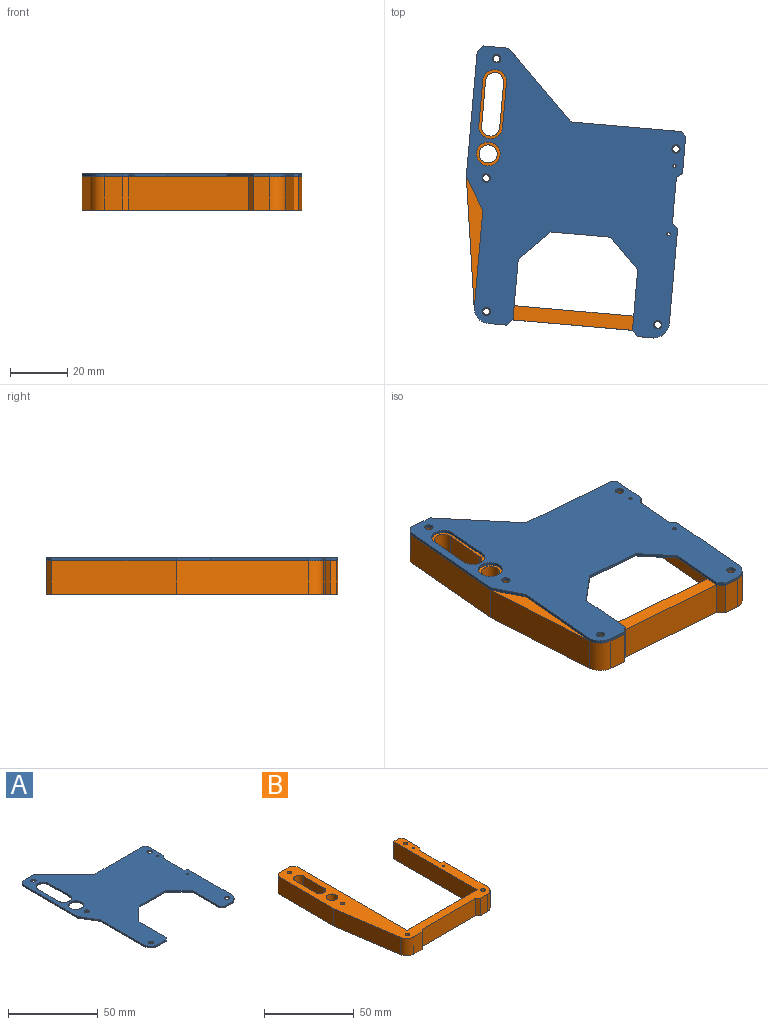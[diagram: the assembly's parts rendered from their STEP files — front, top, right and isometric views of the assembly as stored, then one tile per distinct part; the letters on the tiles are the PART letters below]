
ASSEMBLY  parts=2 mates=1
PART A: 38 faces, bbox 75.4x96.8x1 mm
  f0: plane 5.68x1mm, normal (0,-1,0), area 5.7mm2, adj f2,f3,f15,f37
  f1: plane 12.99x1mm, normal (1,0,0), area 13mm2, adj f2,f3,f17,f28
  f2: plane 96.75x75.4mm, normal (0,0,1), area 4089.1mm2, adj f0,f1,f4,f5,f6,f7,f8,f9
  f3: plane 96.75x75.4mm, normal (0,0,-1), area 4089.1mm2, adj f0,f1,f4,f5,f6,f7,f8,f9
  f4: cylinder r=4.17mm len=8.35mm, axis (0,0,-1), area 13.1mm2, adj f2,f3,f5,f19
  f5: plane 16x1mm, normal (-1,0,0), area 16mm2, adj f2,f3,f4,f6
  f6: cylinder r=4.17mm len=8.35mm, axis (0,0,-1), area 13.1mm2, adj f2,f3,f5,f19
  f7: plane 23.85x23.85mm, normal (0.71,0.71,0), area 33.7mm2, adj f2,f3,f8,f26
  f8: plane 8.87x1mm, normal (0,1,0), area 8.9mm2, adj f2,f3,f7,f9
  f9: plane 2.08x2.08mm, normal (-0.71,0.71,0), area 2.9mm2, adj f2,f3,f8,f10
  f10: plane 43.98x1mm, normal (-1,0,0), area 44mm2, adj f2,f3,f9,f11
  f11: plane 11.36x6.81mm, normal (-0.86,-0.51,0), area 13.2mm2, adj f2,f3,f10,f12
  f12: plane 34.66x1mm, normal (-1,0,0), area 34.7mm2, adj f2,f3,f11,f13
  f13: cylinder r=5.48mm len=5.42mm, axis (0,0,-1), area 7.8mm2, adj f2,f3,f12,f14
  f14: plane 6.44x1mm, normal (0,-1,0), area 6.4mm2, adj f2,f3,f13,f36
  f15: cylinder r=5.48mm len=5.46mm, axis (0,0,-1), area 8.1mm2, adj f0,f2,f3,f16
  f16: plane 33.56x1mm, normal (1,0,0), area 33.6mm2, adj f2,f3,f15,f30
  f17: plane 1.53x1.53mm, normal (0.71,0.71,0), area 2.2mm2, adj f1,f2,f3,f26
  f18: cylinder r=0.57mm len=1.15mm, axis (0,0,-1), area 3.6mm2, adj f2,f3
  f19: plane 16x1mm, normal (1,0,0), area 16mm2, adj f2,f3,f4,f6
  f20: cylinder r=1.45mm len=2.9mm, axis (0,0,-1), area 9.1mm2, adj f2,f3
  f21: cylinder r=1.45mm len=2.9mm, axis (0,0,-1), area 9.1mm2, adj f2,f3
  f22: cylinder r=1.45mm len=2.9mm, axis (0,0,-1), area 9.1mm2, adj f2,f3
  f23: cylinder r=1.45mm len=2.9mm, axis (0,0,-1), area 9.1mm2, adj f2,f3
  f24: cylinder r=1.45mm len=2.9mm, axis (0,0,-1), area 9.1mm2, adj f2,f3
  f25: cylinder r=4.17mm len=8.35mm, axis (0,0,-1), area 26.2mm2, adj f2,f3
  f26: plane 39.08x1mm, normal (0,1,0), area 39.1mm2, adj f2,f3,f7,f17
  f27: cylinder r=0.57mm len=1.15mm, axis (0,0,-1), area 3.6mm2, adj f2,f3
  f28: plane 2x1.68mm, normal (0.64,-0.76,0), area 2.6mm2, adj f1,f2,f3,f29
  f29: plane 16x1mm, normal (1,0,0), area 16mm2, adj f2,f3,f28,f30
  f30: plane 2x1.68mm, normal (0.64,0.76,0), area 2.6mm2, adj f2,f3,f16,f29
  f31: plane 21.35x1mm, normal (1,0,0), area 21.4mm2, adj f2,f3,f33,f36
  f32: plane 21.35x1mm, normal (-1,0,0), area 21.4mm2, adj f2,f3,f34,f37
  f33: plane 10.5x10.5mm, normal (0.71,-0.71,0), area 14.9mm2, adj f2,f3,f31,f35
  f34: plane 10.5x10.5mm, normal (-0.71,-0.71,0), area 14.9mm2, adj f2,f3,f32,f35
  f35: plane 21.04x1mm, normal (0,-1,0), area 21mm2, adj f2,f3,f33,f34
  f36: plane 2x2mm, normal (0.71,-0.71,0), area 2.8mm2, adj f2,f3,f14,f31
  f37: plane 2x2mm, normal (-0.71,-0.71,0), area 2.8mm2, adj f0,f2,f3,f32
PART B: 38 faces, bbox 75.4x96.8x11.8 mm
  f0: plane 11.8x6.44mm, normal (0,-1,0), area 76mm2, adj f2,f3,f4,f35
  f1: plane 12.99x11.8mm, normal (1,0,0), area 153.3mm2, adj f2,f3,f8,f32
  f2: plane 96.75x75.4mm, normal (0,0,1), area 1657.7mm2, adj f0,f1,f4,f5,f6,f7,f8,f9
  f3: plane 96.75x75.4mm, normal (0,0,-1), area 1657.7mm2, adj f0,f1,f4,f5,f6,f7,f8,f9
  f4: cylinder r=5.48mm len=11.8mm, axis (0,0,-1), area 92.1mm2, adj f0,f2,f3,f31
  f5: plane 11.8x5.68mm, normal (0,-1,0), area 67mm2, adj f2,f3,f6,f36
  f6: cylinder r=5.48mm len=11.8mm, axis (0,0,-1), area 95.9mm2, adj f2,f3,f5,f7
  f7: plane 33.56x11.8mm, normal (1,0,0), area 396mm2, adj f2,f3,f6,f34
  f8: plane 11.8x1.53mm, normal (0.71,0.71,0), area 25.5mm2, adj f1,f2,f3,f9
  f9: plane 11.8x4.47mm, normal (0,1,0), area 52.8mm2, adj f2,f3,f8,f10
  f10: plane 65.4x11.8mm, normal (-1,0,0), area 771.8mm2, adj f2,f3,f9,f11
  f11: cylinder r=0.5mm len=11.8mm, axis (0,0,-1), area 9.3mm2, adj f2,f3,f10,f12
  f12: plane 54.4x11.8mm, normal (0,1,0), area 641.9mm2, adj f2,f3,f11,f13
  f13: cylinder r=0.5mm len=11.8mm, axis (0,0,-1), area 9.3mm2, adj f2,f3,f12,f14
  f14: plane 86.2x11.8mm, normal (1,0,0), area 1017.2mm2, adj f2,f3,f13,f15
  f15: plane 11.8x3.05mm, normal (0.71,0.71,0), area 51mm2, adj f2,f3,f14,f16
  f16: plane 11.8x8.87mm, normal (0,1,0), area 104.6mm2, adj f2,f3,f15,f17
  f17: plane 11.8x2.08mm, normal (-0.71,0.71,0), area 34.7mm2, adj f2,f3,f16,f18
  f18: plane 43.98x11.8mm, normal (-1,0,0), area 518.9mm2, adj f2,f3,f17,f31
  f19: plane 16x11.8mm, normal (1,0,0), area 188.8mm2, adj f2,f3,f20,f25
  f20: cylinder r=3.17mm len=11.8mm, axis (0,0,-1), area 117.7mm2, adj f2,f3,f19,f21
  f21: plane 16x11.8mm, normal (-1,0,0), area 188.8mm2, adj f2,f3,f20,f25
  f22: cylinder r=1.2mm len=11.8mm, axis (0,0,-1), area 89mm2, adj f2,f3
  f23: cylinder r=3.17mm len=11.8mm, axis (0,0,-1), area 235.4mm2, adj f2,f3
  f24: cylinder r=1.2mm len=11.8mm, axis (0,0,-1), area 89mm2, adj f2,f3
  f25: cylinder r=3.17mm len=11.8mm, axis (0,0,-1), area 117.7mm2, adj f2,f3,f19,f21
  f26: cylinder r=1.2mm len=11.8mm, axis (0,0,-1), area 89mm2, adj f2,f3
  f27: cylinder r=1.2mm len=11.8mm, axis (0,0,-1), area 89mm2, adj f2,f3
  f28: cylinder r=0.57mm len=11.8mm, axis (0,0,-1), area 42.6mm2, adj f2,f3
  f29: cylinder r=0.57mm len=11.8mm, axis (0,0,-1), area 42.6mm2, adj f2,f3
  f30: cylinder r=1.2mm len=11.8mm, axis (0,0,-1), area 89mm2, adj f2,f3
  f31: plane 46.02x11.8mm, normal (-0.99,-0.15,0), area 549mm2, adj f2,f3,f4,f18
  f32: plane 11.8x2mm, normal (0.64,-0.76,0), area 30.9mm2, adj f1,f2,f3,f33
  f33: plane 16x11.8mm, normal (1,0,0), area 188.8mm2, adj f2,f3,f32,f34
  f34: plane 11.8x2mm, normal (0.64,0.76,0), area 30.9mm2, adj f2,f3,f7,f33
  f35: plane 11.8x2mm, normal (0.71,-0.71,0), area 33.4mm2, adj f0,f2,f3,f37
  f36: plane 11.8x2mm, normal (-0.71,-0.71,0), area 33.4mm2, adj f2,f3,f5,f37
  f37: plane 42.05x11.8mm, normal (0,-1,0), area 496.1mm2, adj f2,f3,f35,f36
PLACE A rot(axis=(0,0,-1),5deg) t=(-16.84,-17.09,5.09)mm
PLACE B rot(axis=(0,0,-1),5deg) t=(-16.84,-17.09,5.09)mm
MATE fastened B.f24 <-> A.f22  axis (0,0,1) through (-51.33,-60.8,22.49)mm
